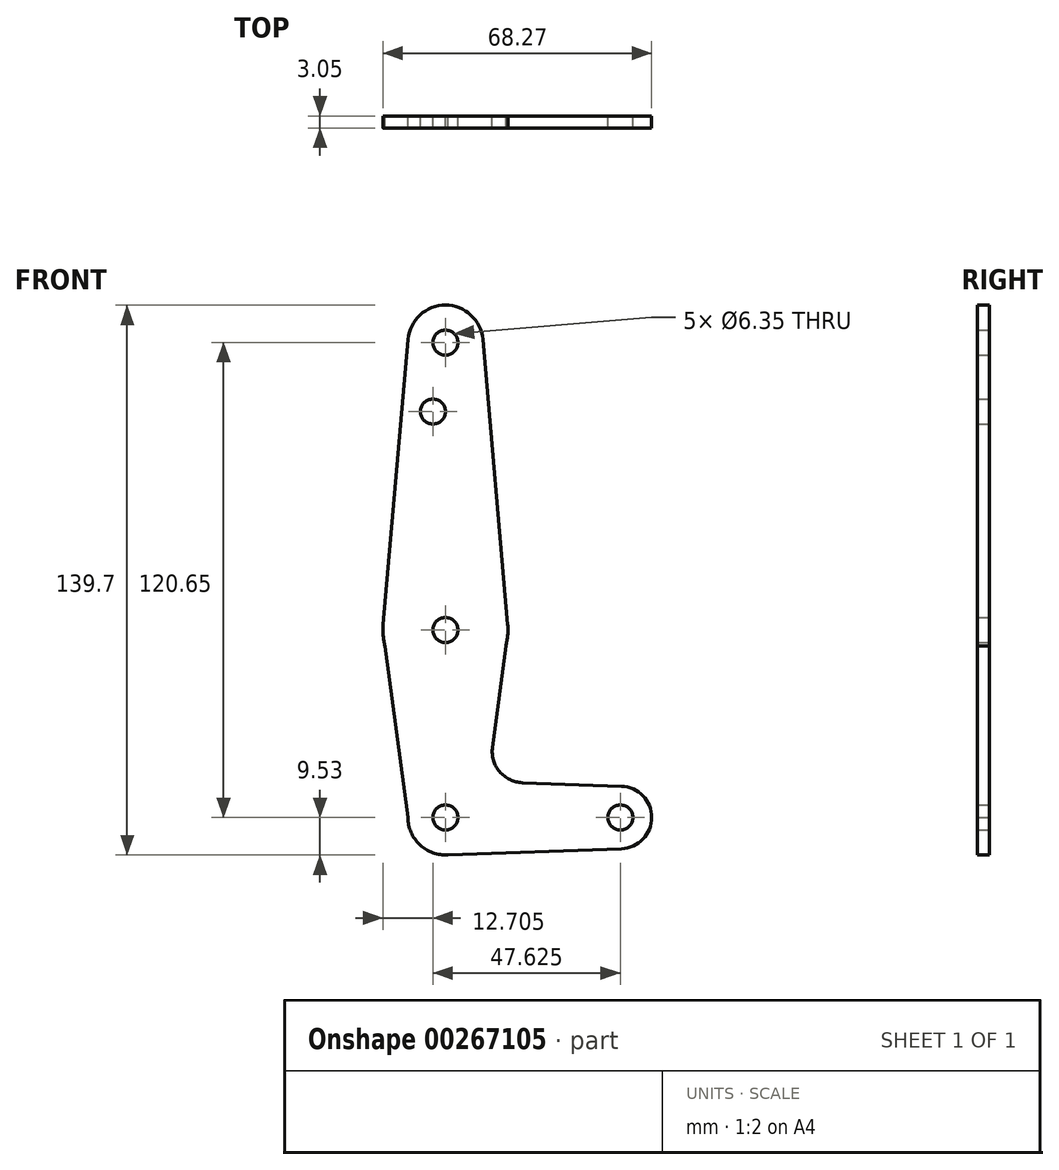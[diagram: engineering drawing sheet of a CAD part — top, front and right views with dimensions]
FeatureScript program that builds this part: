
annotation { "Feature Type Name" : "Feature", "Feature Type Description" : "" }
export const myFeature = defineFeature(function(context is Context, id is Id, definition is map)
    precondition{}
    {
        {
            var Q0;
            Q0=qCreatedBy(makeId("Front.planeOp"),FACE);
            var sketch = newSketch(context, id + "F0", { "sketchPlane" : qUnion([Q0])});
            skLineSegment(sketch, "E0", {"start": v(0, 57.15) * mm, "end": v(0, 0) * mm});
            skLineSegment(sketch, "E1", {"start": v(0, 0) * mm, "end": v(0, -63.5) * mm});
            skLineSegment(sketch, "E2", {"start": v(0, -63.5) * mm, "end": v(44.45, -63.5) * mm});
            skCircle(sketch, "E3", {"center": v(0, 57.15) * mm, "radius": 9.53 * mm});
            skCircle(sketch, "E4", {"center": v(0, -15.88) * mm, "radius": 15.88 * mm});
            skCircle(sketch, "E5", {"center": v(0, -63.5) * mm, "radius": 9.53 * mm});
            skCircle(sketch, "E6", {"center": v(44.45, -63.5) * mm, "radius": 7.94 * mm});
            skLineSegment(sketch, "E7", {"start": v(9.49, 57.98) * mm, "end": v(15.81, -14.5) * mm});
            skLineSegment(sketch, "E8", {"start": v(-9.49, 57.98) * mm, "end": v(-15.81, -14.5) * mm});
            skLineSegment(sketch, "E9", {"start": v(0, -73.03) * mm, "end": v(44.73, -71.43) * mm});
            skLineSegment(sketch, "E10", {"start": v(15.87, -15.88) * mm, "end": v(11.95, -45.68) * mm});
            skCircle(sketch, "E11", {"center": v(0, 57.15) * mm, "radius": 3.18 * mm});
            skCircle(sketch, "E12", {"center": v(0, -15.88) * mm, "radius": 3.18 * mm});
            skCircle(sketch, "E13", {"center": v(0, -63.5) * mm, "radius": 3.18 * mm});
            skPoint(sketch, "E14.newPointA", {"position": v(9.6, -63.5) * mm});
            skArc(sketch, "E14.filletArc", {"start": v(11.95, -45.68) * mm, "mid": v(13.76, -51.85) * mm, "end": v(19.55, -54.66) * mm});
            skLineSegment(sketch, "E15", {"start": v(-15.88, -15.88) * mm, "end": v(-9.53, -63.5) * mm});
            skCircle(sketch, "E16", {"center": v(44.45, -63.5) * mm, "radius": 3.18 * mm});
            skCircle(sketch, "E17", {"center": v(-3.18, 39.64) * mm, "radius": 3.18 * mm});
            skLineSegment(sketch, "E18", {"start": v(44.73, -55.57) * mm, "end": v(19.55, -54.66) * mm});
            skSolve(sketch);
        }
        {
            var Q0;
            {var subQ3=sQuery(id+"F0.wireOp",EDGE,"E7");Q0=makeQuery(id+"F0.imprint","IMPRINT",FACE,{"disambiguationData":[TD([[makeQuery(id+"F0.imprint","IMPRINT",EDGE,{"derivedFrom":subQ3}),-1.0]])]});}
            var Q1;
            {var subQ0=sQuery(id+"F0.wireOp",EDGE,"E4");var subQ1=sQuery(id+"F0.wireOp",EDGE,"E1");var subQ2=makeQuery(id+"F0.imprint","INTERSECT",VERTEX,{"derivedFrom":[subQ1,subQ0]});Q1=makeQuery(id+"F0.imprint","IMPRINT",FACE,{"disambiguationData":[TD([[makeQuery(id+"F0.imprint","IMPRINT",EDGE,{"disambiguationData":[TD([[subQ2,-1.0]])],"derivedFrom":subQ1}),-1.0]])]});}
            var Q2;
            {var subQ0=sQuery(id+"F0.wireOp",EDGE,"E6");var subQ1=sQuery(id+"F0.wireOp",EDGE,"E2");var subQ2=makeQuery(id+"F0.imprint","INTERSECT",VERTEX,{"derivedFrom":[subQ1,subQ0]});Q2=makeQuery(id+"F0.imprint","IMPRINT",FACE,{"disambiguationData":[TD([[makeQuery(id+"F0.imprint","IMPRINT",EDGE,{"disambiguationData":[TD([[subQ2,1.0]])],"derivedFrom":subQ1}),-1.0]])]});}
            var Q3;
            Q3=makeQuery(id+"F0.imprint","IMPRINT",FACE,{"disambiguationData":[TD([[makeQuery(id+"F0.imprint","IMPRINT",EDGE,{"derivedFrom":sQuery(id+"F0.wireOp",EDGE,"E11")}),-1.0]])]});
            var Q4;
            Q4=makeQuery(id+"F0.imprint","IMPRINT",FACE,{"disambiguationData":[TD([[makeQuery(id+"F0.imprint","IMPRINT",EDGE,{"derivedFrom":sQuery(id+"F0.wireOp",EDGE,"E16")}),-1.0]])]});
            var Q5;
            {var subQ0=sQuery(id+"F0.wireOp",EDGE,"E8");Q5=makeQuery(id+"F0.imprint","IMPRINT",FACE,{"disambiguationData":[TD([[makeQuery(id+"F0.imprint","IMPRINT",EDGE,{"derivedFrom":subQ0}),1.0]])]});}
            var Q6;
            {var subQ1=sQuery(id+"F0.wireOp",EDGE,"E1");var subQ6=sQuery(id+"F0.wireOp",EDGE,"E12");var subQ7=makeQuery(id+"F0.imprint","INTERSECT",VERTEX,{"disambiguationData":[OD(1.0)],"derivedFrom":[subQ1,subQ6]});Q6=makeQuery(id+"F0.imprint","IMPRINT",FACE,{"disambiguationData":[TD([[makeQuery(id+"F0.imprint","IMPRINT",EDGE,{"disambiguationData":[TD([[subQ7,-1.0]])],"derivedFrom":subQ1}),1.0]])]});}
            var Q7;
            {var subQ0=sQuery(id+"F0.wireOp",EDGE,"E12");var subQ1=sQuery(id+"F0.wireOp",EDGE,"E1");var subQ2=makeQuery(id+"F0.imprint","INTERSECT",VERTEX,{"disambiguationData":[OD(1.0)],"derivedFrom":[subQ1,subQ0]});Q7=makeQuery(id+"F0.imprint","IMPRINT",FACE,{"disambiguationData":[TD([[makeQuery(id+"F0.imprint","IMPRINT",EDGE,{"disambiguationData":[TD([[subQ2,-1.0]])],"derivedFrom":subQ1}),-1.0]])]});}
            var Q8;
            {var subQ5=sQuery(id+"F0.wireOp",EDGE,"E14.filletArc");Q8=makeQuery(id+"F0.imprint","IMPRINT",FACE,{"disambiguationData":[TD([[makeQuery(id+"F0.imprint","IMPRINT",EDGE,{"derivedFrom":subQ5}),-1.0]])]});}
            var Q9;
            {var subQ0=sQuery(id+"F0.wireOp",EDGE,"E5");var subQ2=sQuery(id+"F0.wireOp",EDGE,"E1");var subQ3=makeQuery(id+"F0.imprint","INTERSECT",VERTEX,{"derivedFrom":[subQ2,subQ0]});Q9=makeQuery(id+"F0.imprint","IMPRINT",FACE,{"disambiguationData":[TD([[makeQuery(id+"F0.imprint","IMPRINT",EDGE,{"disambiguationData":[TD([[subQ3,-1.0]])],"derivedFrom":subQ2}),-1.0]])]});}
            var Q10;
            {var subQ0=sQuery(id+"F0.wireOp",EDGE,"E5");var subQ1=sQuery(id+"F0.wireOp",EDGE,"E1");var subQ2=makeQuery(id+"F0.imprint","INTERSECT",VERTEX,{"derivedFrom":[subQ1,subQ0]});Q10=makeQuery(id+"F0.imprint","IMPRINT",FACE,{"disambiguationData":[TD([[makeQuery(id+"F0.imprint","IMPRINT",EDGE,{"disambiguationData":[TD([[subQ2,-1.0]])],"derivedFrom":subQ1}),1.0]])]});}
            var Q11;
            Q11 = qSketchRegion(id + "F0", true);
            extrude(context, id + "F1", {"entities" : qUnion([Q0, Q1, Q2, Q3, Q4, Q5, Q6, Q7, Q8, Q9, Q10, Q11]), "depth" : 3.05 * mm});
        }
    });
